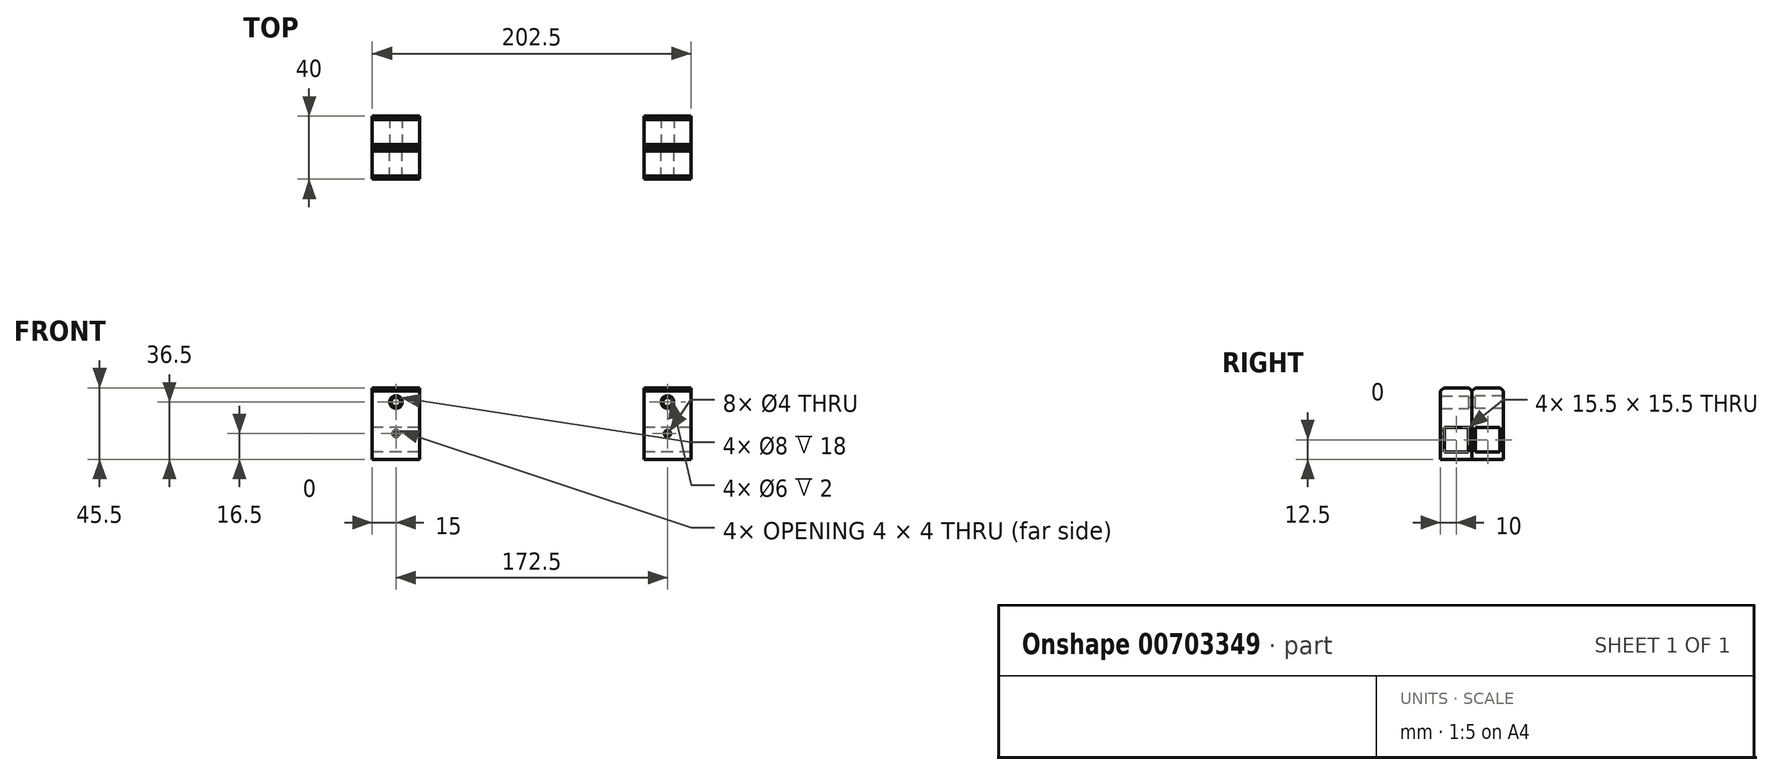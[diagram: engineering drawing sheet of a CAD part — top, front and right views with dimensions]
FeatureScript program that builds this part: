
annotation { "Feature Type Name" : "Feature", "Feature Type Description" : "" }
export const myFeature = defineFeature(function(context is Context, id is Id, definition is map)
    precondition{}
    {
        {
            var Q0;
            Q0=qCreatedBy(makeId("Front.planeOp"),FACE);
            var sketch = newSketch(context, id + "F0", { "sketchPlane" : qUnion([Q0])});
            skCircle(sketch, "E0", {"center": v(-75, 0) * mm, "radius": 4 * mm});
            skCircle(sketch, "E1", {"center": v(97.5, 0) * mm, "radius": 4 * mm});
            skLineSegment(sketch, "E2.bottom", {"start": v(-90, 9) * mm, "end": v(-60, 9) * mm});
            skLineSegment(sketch, "E2.top", {"start": v(-90, -45) * mm, "end": v(-60, -45) * mm});
            skLineSegment(sketch, "E2.left", {"start": v(-90, 9) * mm, "end": v(-90, -45) * mm});
            skLineSegment(sketch, "E2.right", {"start": v(-60, 9) * mm, "end": v(-60, -45) * mm});
            skLineSegment(sketch, "E3.bottom", {"start": v(82.5, -45) * mm, "end": v(112.5, -45) * mm});
            skLineSegment(sketch, "E3.top", {"start": v(82.5, 9) * mm, "end": v(112.5, 9) * mm});
            skLineSegment(sketch, "E3.left", {"start": v(82.5, -45) * mm, "end": v(82.5, 9) * mm});
            skLineSegment(sketch, "E3.right", {"start": v(112.5, -45) * mm, "end": v(112.5, 9) * mm});
            skCircle(sketch, "E4", {"center": v(-75, -20) * mm, "radius": 2 * mm});
            skCircle(sketch, "E5", {"center": v(97.5, -20) * mm, "radius": 2 * mm});
            skCircle(sketch, "E6", {"center": v(-75, 0) * mm, "radius": 3 * mm});
            skCircle(sketch, "E7", {"center": v(97.5, 0) * mm, "radius": 3 * mm});
            skSolve(sketch);
        }
        {
            var Q0;
            Q0=makeQuery(id+"F0.imprint","IMPRINT",FACE,{"disambiguationData":[TD([[makeQuery(id+"F0.imprint","IMPRINT",EDGE,{"derivedFrom":sQuery(id+"F0.wireOp",EDGE,"E0")}),-1.0]])]});
            var Q1;
            Q1=makeQuery(id+"F0.imprint","IMPRINT",FACE,{"disambiguationData":[TD([[makeQuery(id+"F0.imprint","IMPRINT",EDGE,{"derivedFrom":sQuery(id+"F0.wireOp",EDGE,"E1")}),-1.0]])]});
            extrude(context, id + "F1", {"entities" : qUnion([Q0, Q1]), "oppositeDirection" : true, "depth" : 20 * mm, "offsetDistance" : 25 * mm});
        }
        {
            var Q0;
            Q0=makeQuery(id+"F1.opExtrude","SWEPT_FACE",FACE,{"disambiguationData":[OSD([sQuery(id+"F0.wireOp",EDGE,"E2.left")])]});
            var sketch = newSketch(context, id + "F2", { "sketchPlane" : qUnion([Q0])});
            skLineSegment(sketch, "E8", {"start": v(-10, 9) * mm, "end": v(-10, -45) * mm, "construction": true});
            skLineSegment(sketch, "E9.bottom", {"start": v(-17.75, -16.25) * mm, "end": v(-2.25, -16.25) * mm});
            skLineSegment(sketch, "E9.top", {"start": v(-17.75, -31.75) * mm, "end": v(-2.25, -31.75) * mm});
            skLineSegment(sketch, "E9.left", {"start": v(-17.75, -16.25) * mm, "end": v(-17.75, -31.75) * mm});
            skLineSegment(sketch, "E9.right", {"start": v(-2.25, -16.25) * mm, "end": v(-2.25, -31.75) * mm});
            skPoint(sketch, "E9.middle", {"position": v(-10, -24) * mm});
            skPoint(sketch, "E10", {"position": v(-10, 0) * mm});
            skLineSegment(sketch, "E11", {"start": v(-20, -36.5) * mm, "end": v(0, -36.5) * mm});
            skSolve(sketch);
        }
        {
            var Q0;
            Q0=makeQuery(id+"F2.imprint","IMPRINT",FACE,{"disambiguationData":[TD([[makeQuery(id+"F2.imprint","IMPRINT",EDGE,{"derivedFrom":sQuery(id+"F2.wireOp",EDGE,"E9.bottom")}),-1.0]])]});
            var Q1;
            {var subQ0=sQuery(id+"F2.wireOp",EDGE,"E11");Q1=makeQuery(id+"F2.imprint","IMPRINT",FACE,{"disambiguationData":[TD([[makeQuery(id+"F2.imprint","IMPRINT",EDGE,{"derivedFrom":subQ0}),-1.0]])]});}
            extrude(context, id + "F3", {"entities" : qUnion([Q0, Q1]), "operationType" : NewBodyOperationType.REMOVE, "endBound" : BoundingType.THROUGH_ALL, "oppositeDirection" : true, "depth" : 25 * mm, "offsetDistance" : 25 * mm});
        }
        {
            var Q0;
            Q0=makeQuery(id+"F0.imprint","IMPRINT",FACE,{"disambiguationData":[TD([[makeQuery(id+"F0.imprint","IMPRINT",EDGE,{"derivedFrom":sQuery(id+"F0.wireOp",EDGE,"E1")}),1.0]])]});
            var Q1;
            Q1=makeQuery(id+"F0.imprint","IMPRINT",FACE,{"disambiguationData":[TD([[makeQuery(id+"F0.imprint","IMPRINT",EDGE,{"derivedFrom":sQuery(id+"F0.wireOp",EDGE,"E0")}),1.0]])]});
            extrude(context, id + "F4", {"entities" : qUnion([Q0, Q1]), "operationType" : NewBodyOperationType.ADD, "oppositeDirection" : true, "depth" : 2 * mm, "offsetDistance" : 25 * mm});
        }
        {
            var Q0;
            Q0=makeQuery(id+"F1.opExtrude","CAP_EDGE",EDGE,{"disambiguationData":[OSD([sQuery(id+"F0.wireOp",EDGE,"E2.bottom")])],"isStart":false});
            var Q1;
            {var subQ0=sQuery(id+"F0.wireOp",EDGE,"E2.left");var subQ1=sQuery(id+"F2.wireOp",EDGE,"E11");Q1=makeQuery(id+"F3.boolean.opBoolean","COPY",EDGE,{"disambiguationData":[topologyDisambiguationEdgeConnected([makeQuery(id+"F1.opExtrude","CAP_FACE",FACE,{"disambiguationData":[OSD([sQuery(id+"F0.wireOp",EDGE,"E0"),sQuery(id+"F0.wireOp",EDGE,"E2.bottom"),sQuery(id+"F0.wireOp",EDGE,"E2.top"),subQ0,sQuery(id+"F0.wireOp",EDGE,"E2.right"),sQuery(id+"F0.wireOp",EDGE,"E4")])],"isStart":false})])],"derivedFrom":makeQuery(id+"F3.opExtrude","SWEPT_EDGE",EDGE,{"disambiguationData":[OSD([subQ0,subQ1]),TDD([makeQuery(id+"F2.imprint","INTERSECT",VERTEX,{"derivedFrom":[makeQuery(id+"F1.opExtrude","CAP_EDGE",EDGE,{"disambiguationData":[OSD([subQ0])],"isStart":false}),subQ1]})])]})});}
            var Q2;
            {var subQ0=sQuery(id+"F0.wireOp",EDGE,"E2.left");var subQ1=sQuery(id+"F2.wireOp",EDGE,"E11");Q2=makeQuery(id+"F3.boolean.opBoolean","COPY",EDGE,{"disambiguationData":[topologyDisambiguationEdgeConnected([makeQuery(id+"F1.opExtrude","CAP_FACE",FACE,{"disambiguationData":[OSD([sQuery(id+"F0.wireOp",EDGE,"E0"),sQuery(id+"F0.wireOp",EDGE,"E2.bottom"),sQuery(id+"F0.wireOp",EDGE,"E2.top"),subQ0,sQuery(id+"F0.wireOp",EDGE,"E2.right"),sQuery(id+"F0.wireOp",EDGE,"E4")])],"isStart":true})])],"derivedFrom":makeQuery(id+"F3.opExtrude","SWEPT_EDGE",EDGE,{"disambiguationData":[OSD([subQ0,subQ1]),TDD([makeQuery(id+"F2.imprint","INTERSECT",VERTEX,{"derivedFrom":[makeQuery(id+"F1.opExtrude","CAP_EDGE",EDGE,{"disambiguationData":[OSD([subQ0])],"isStart":true}),subQ1]})])]})});}
            var Q3;
            Q3=makeQuery(id+"F1.opExtrude","CAP_EDGE",EDGE,{"disambiguationData":[OSD([sQuery(id+"F0.wireOp",EDGE,"E2.bottom")])],"isStart":true});
            var Q4;
            Q4=makeQuery(id+"F1.opExtrude","CAP_EDGE",EDGE,{"disambiguationData":[OSD([sQuery(id+"F0.wireOp",EDGE,"E3.top")])],"isStart":true});
            var Q5;
            {var subQ0=sQuery(id+"F2.wireOp",EDGE,"E11");var subQ1=sQuery(id+"F0.wireOp",EDGE,"E2.left");Q5=makeQuery(id+"F3.boolean.opBoolean","COPY",EDGE,{"disambiguationData":[topologyDisambiguationEdgeConnected([makeQuery(id+"F1.opExtrude","CAP_FACE",FACE,{"disambiguationData":[OSD([sQuery(id+"F0.wireOp",EDGE,"E1"),sQuery(id+"F0.wireOp",EDGE,"E3.bottom"),sQuery(id+"F0.wireOp",EDGE,"E3.top"),sQuery(id+"F0.wireOp",EDGE,"E3.left"),sQuery(id+"F0.wireOp",EDGE,"E3.right"),sQuery(id+"F0.wireOp",EDGE,"E5")])],"isStart":true})])],"derivedFrom":makeQuery(id+"F3.opExtrude","SWEPT_EDGE",EDGE,{"disambiguationData":[OSD([subQ1,subQ0]),TDD([makeQuery(id+"F2.imprint","INTERSECT",VERTEX,{"derivedFrom":[makeQuery(id+"F1.opExtrude","CAP_EDGE",EDGE,{"disambiguationData":[OSD([subQ1])],"isStart":true}),subQ0]})])]})});}
            var Q6;
            Q6=makeQuery(id+"F1.opExtrude","CAP_EDGE",EDGE,{"disambiguationData":[OSD([sQuery(id+"F0.wireOp",EDGE,"E3.top")])],"isStart":false});
            var Q7;
            {var subQ0=sQuery(id+"F2.wireOp",EDGE,"E11");var subQ1=sQuery(id+"F0.wireOp",EDGE,"E2.left");Q7=makeQuery(id+"F3.boolean.opBoolean","COPY",EDGE,{"disambiguationData":[topologyDisambiguationEdgeConnected([makeQuery(id+"F1.opExtrude","CAP_FACE",FACE,{"disambiguationData":[OSD([sQuery(id+"F0.wireOp",EDGE,"E1"),sQuery(id+"F0.wireOp",EDGE,"E3.bottom"),sQuery(id+"F0.wireOp",EDGE,"E3.top"),sQuery(id+"F0.wireOp",EDGE,"E3.left"),sQuery(id+"F0.wireOp",EDGE,"E3.right"),sQuery(id+"F0.wireOp",EDGE,"E5")])],"isStart":false})])],"derivedFrom":makeQuery(id+"F3.opExtrude","SWEPT_EDGE",EDGE,{"disambiguationData":[OSD([subQ1,subQ0]),TDD([makeQuery(id+"F2.imprint","INTERSECT",VERTEX,{"derivedFrom":[makeQuery(id+"F1.opExtrude","CAP_EDGE",EDGE,{"disambiguationData":[OSD([subQ1])],"isStart":false}),subQ0]})])]})});}
            chamfer(context, id + "F5", {"entities" : qUnion([Q0, Q1, Q2, Q3, Q4, Q5, Q6, Q7]), "width" : 2 * mm, "tangentPropagation" : true});
        }
        {
            var Q0;
            Q0=makeQuery(id+"F1.opExtrude","SWEPT_BODY",BODY,{"disambiguationData":[OSD([sQuery(id+"F0.wireOp",EDGE,"E0"),sQuery(id+"F0.wireOp",EDGE,"E2.bottom"),sQuery(id+"F0.wireOp",EDGE,"E2.top"),sQuery(id+"F0.wireOp",EDGE,"E2.left"),sQuery(id+"F0.wireOp",EDGE,"E2.right"),sQuery(id+"F0.wireOp",EDGE,"E4")])]});
            var Q1;
            Q1=makeQuery(id+"F1.opExtrude","SWEPT_BODY",BODY,{"disambiguationData":[OSD([sQuery(id+"F0.wireOp",EDGE,"E1"),sQuery(id+"F0.wireOp",EDGE,"E3.bottom"),sQuery(id+"F0.wireOp",EDGE,"E3.top"),sQuery(id+"F0.wireOp",EDGE,"E3.left"),sQuery(id+"F0.wireOp",EDGE,"E3.right"),sQuery(id+"F0.wireOp",EDGE,"E5")])]});
            var Q2;
            Q2=qCreatedBy(makeId("Front.planeOp"),FACE);
            mirror(context, id + "F6", {"entities" : qUnion([Q0, Q1]), "mirrorPlane" : qUnion([Q2])});
        }
    });
